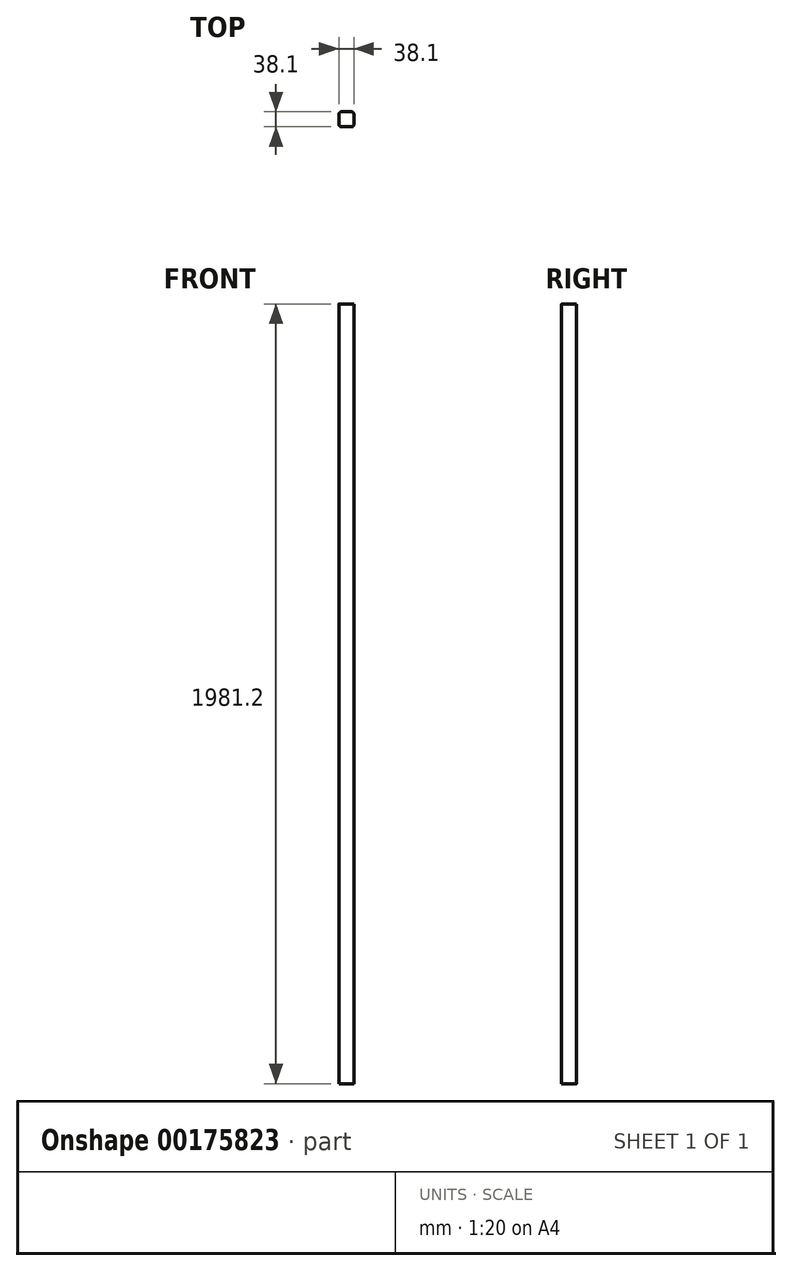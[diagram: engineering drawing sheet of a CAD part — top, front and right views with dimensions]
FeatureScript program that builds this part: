
annotation { "Feature Type Name" : "Feature", "Feature Type Description" : "" }
export const myFeature = defineFeature(function(context is Context, id is Id, definition is map)
    precondition{}
    {
        {
            var Q0;
            Q0=qCreatedBy(makeId("Top.planeOp"),FACE);
            var sketch = newSketch(context, id + "F0", { "sketchPlane" : qUnion([Q0])});
            skLineSegment(sketch, "E0.bottom", {"start": v(12.7, 19.05) * mm, "end": v(-12.7, 19.05) * mm});
            skLineSegment(sketch, "E0.top", {"start": v(12.7, -19.05) * mm, "end": v(-12.7, -19.05) * mm});
            skLineSegment(sketch, "E0.left", {"start": v(19.05, 12.7) * mm, "end": v(19.05, -12.7) * mm});
            skLineSegment(sketch, "E0.right", {"start": v(-19.05, 12.7) * mm, "end": v(-19.05, -12.7) * mm});
            skPoint(sketch, "E0.middle", {"position": v(0, 0) * mm});
            skPoint(sketch, "E1.visualSharp", {"position": v(-19.05, 19.05) * mm});
            skArc(sketch, "E1.filletArc", {"start": v(-12.7, 19.05) * mm, "mid": v(-17.2, 17.2) * mm, "end": v(-19.05, 12.7) * mm});
            skPoint(sketch, "E2.visualSharp", {"position": v(19.05, 19.05) * mm});
            skArc(sketch, "E2.filletArc", {"start": v(19.05, 12.7) * mm, "mid": v(17.2, 17.2) * mm, "end": v(12.7, 19.05) * mm});
            skPoint(sketch, "E3.visualSharp", {"position": v(19.05, -19.05) * mm});
            skArc(sketch, "E3.filletArc", {"start": v(12.7, -19.05) * mm, "mid": v(17.2, -17.2) * mm, "end": v(19.05, -12.7) * mm});
            skPoint(sketch, "E4.visualSharp", {"position": v(-19.05, -19.05) * mm});
            skArc(sketch, "E4.filletArc", {"start": v(-19.05, -12.7) * mm, "mid": v(-17.2, -17.2) * mm, "end": v(-12.7, -19.05) * mm});
            skSolve(sketch);
        }
        {
            var Q0;
            Q0=qSketchRegion(id+"F0",true);
            extrude(context, id + "F1", {"entities" : qUnion([Q0]), "depth" : 1981.2 * mm, "offsetDistance" : 25.4 * mm});
        }
    });
